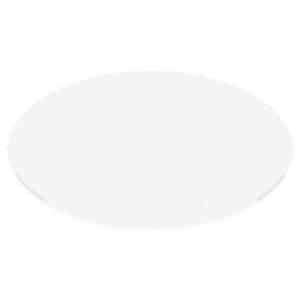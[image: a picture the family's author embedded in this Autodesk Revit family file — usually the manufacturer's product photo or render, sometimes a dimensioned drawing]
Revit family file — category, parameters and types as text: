
# Revit family: sign_110-1340
name_source: partatom
category: Leuchten
revit_build: Autodesk Revit 2016 (Build: 20190508_0715(x64)
units: mm (PartAtom-declared; Revit-internal decimal feet)

## family parameters
Basisbauteil = Fläche
Beim Laden mit Abzugskörper schneiden = Nein
Bemaßung runder Anschluss = Durchmesser verwenden
Gemeinsam genutzt = Nein
Lichtquelle = Nein
Raumberechnungspunkt = Nein
Teiletyp = Normal

## types (1)
- 110-1340-D01-H30 (1 x LED, 1627.38 lm, 12.6 W, 3000K)
    Beschreibung = SIGN
    CIE Flux Codes = 48 79 95 100 58
    Color Rendering = 1B/80…89
    Color Temperature = 3000K
    Height = 0 mm  [stored 0 ft]
    Hersteller = Prolicht
    Lamp Light Flux = 1627.38 lm
    Lamp Power = 12.6 W
    Lamp count = 1
    Lampe = 1 x LED
    Length = 200 mm  [stored 0.656168 ft]
    Luminous efficacy = 75 lm/W
    ModVariant = Nein
    Modell = 110-1340
    Mounting Place = Ceiling
    Mounting Type = Recessed
    Number of Poles = 1
    OnlyDefault = Ja
    Power Factor = 1
    Product Name = SIGN
    Product group = Trimless recessed lights
    ProductGroupID = 411
    Protection Class = Protection class
    Protection Degree = Degree of protection
    RLX_Detail_Level = 1
    RlxData = <blob elided: 79525 chars, md5=54d1b21e>
    Scheinlast = 13 VA
    Socket = socket
    Standby Power = 0 W
    System Light Flux = 949 lm
    System Power = 13 W
    Typenbild = 110-1340.jpg
    Typenkommentare = DIFFUSER Opal (01),LED COLOUR DIR 3000 K (30)
    URL = http://relux.com
    VarID = 110-1340-d01-h30
    Voltage = 0 V
    Vorgabe-Ansicht = 1800 mm
    Weight = 0.00 kg
    Width = 0 mm  [stored 0 ft]

note: [stored X ft] marks values corroborated as IEEE doubles in the binary element streams (Revit-internal decimal feet)

## geometry (parser evidence)
native form markers: Sweep x15
no freeform markers — native parametric forms only
